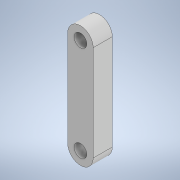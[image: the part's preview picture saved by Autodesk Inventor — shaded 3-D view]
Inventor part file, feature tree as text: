
AUTODESK INVENTOR PART (.ipt)
format: ipt  version: 2021 (Build 250183000, 183)  size: 107,520 bytes
history: native  units: mm
features: extrude x1, sketch x1
ambient origin geometry x8: Origin, YZ Plane, XZ Plane, XY Plane, X Axis, Y Axis, Z Axis, Center Point
bodies: Solid1 (feature_tree)
feature tree (2):
  extrude  "Extrusion1"  Depth=8.0mm
  sketch  "Sketch1"  dims[d0=4.0mm d1=8.0mm d2=4.0mm d3=8.0mm d4=6.0mm d5=0.0mm d6=30.0mm]
